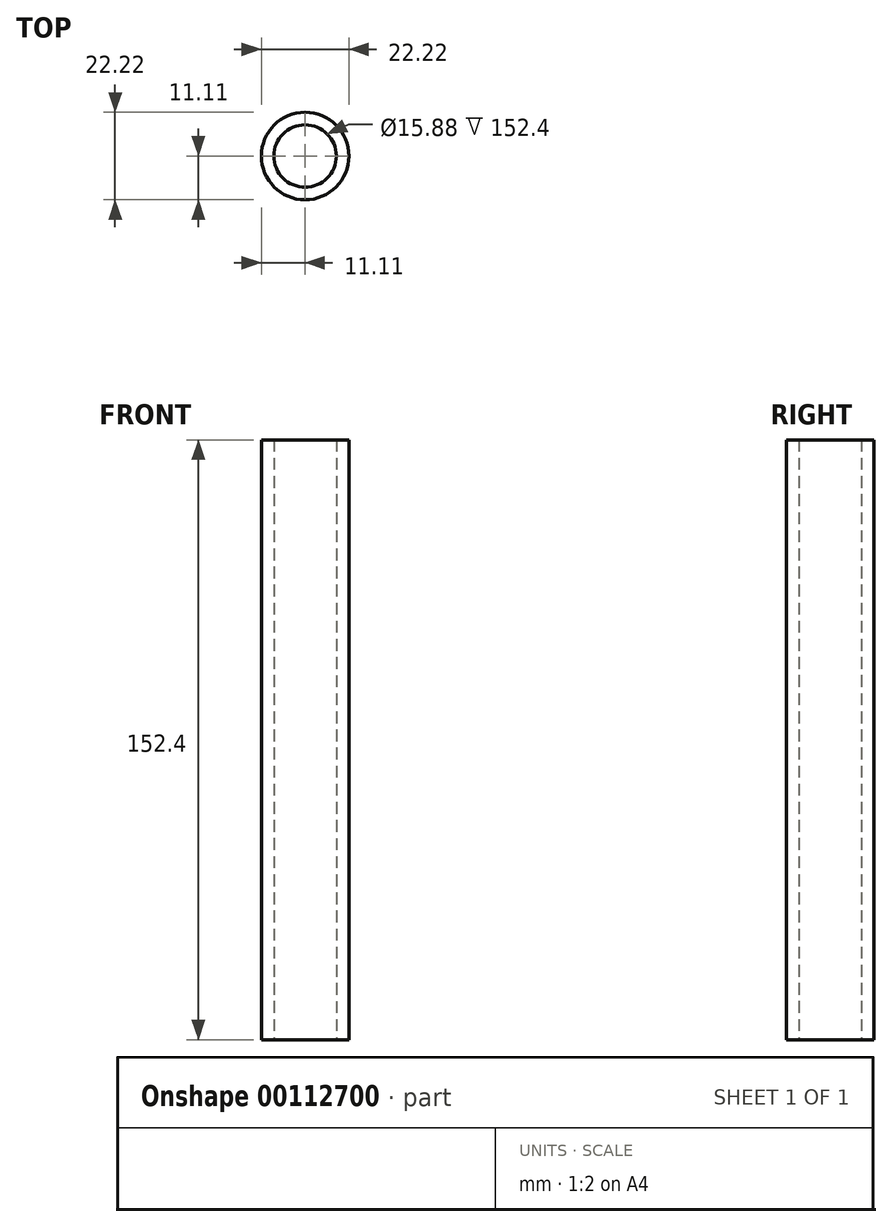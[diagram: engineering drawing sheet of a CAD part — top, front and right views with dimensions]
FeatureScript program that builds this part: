
annotation { "Feature Type Name" : "Feature", "Feature Type Description" : "" }
export const myFeature = defineFeature(function(context is Context, id is Id, definition is map)
    precondition{}
    {
        {
            var Q0;
            Q0=qCreatedBy(makeId("Top.planeOp"),FACE);
            var sketch = newSketch(context, id + "F0", { "sketchPlane" : qUnion([Q0])});
            skCircle(sketch, "E0", {"center": v(0, 0) * mm, "radius": 7.94 * mm});
            skCircle(sketch, "E1", {"center": v(0, 0) * mm, "radius": 11.11 * mm});
            skSolve(sketch);
        }
        {
            var Q0;
            Q0 = qSketchRegion(id + "F0", true);
            extrude(context, id + "F1", {"entities" : qUnion([Q0]), "depth" : 152.4 * mm});
        }
    });
